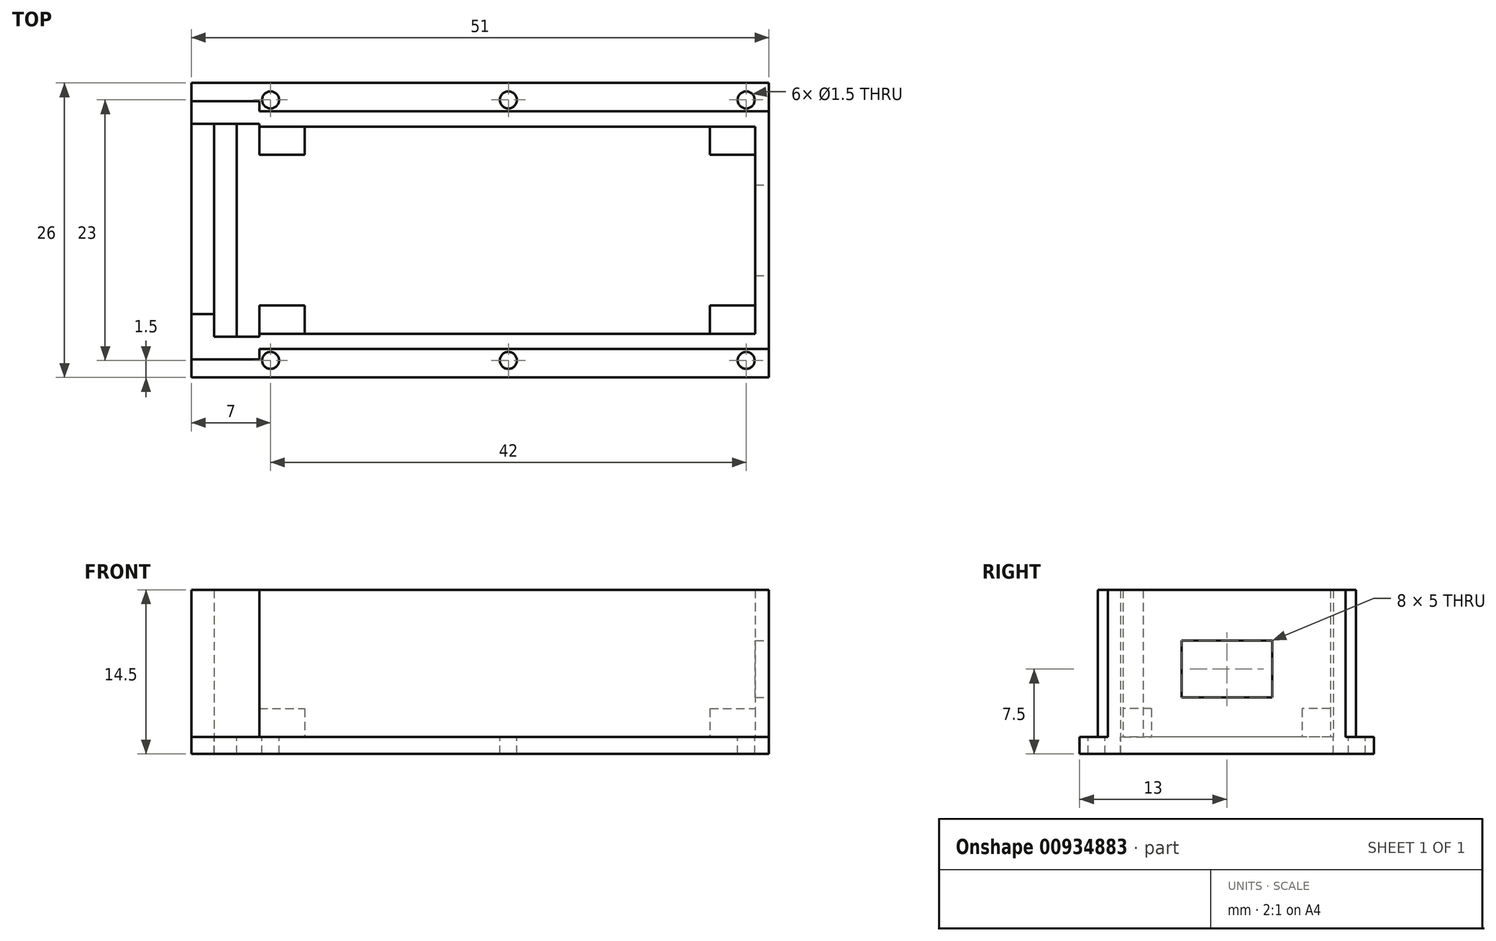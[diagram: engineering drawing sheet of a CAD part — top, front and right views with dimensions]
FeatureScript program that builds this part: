
annotation { "Feature Type Name" : "Feature", "Feature Type Description" : "" }
export const myFeature = defineFeature(function(context is Context, id is Id, definition is map)
    precondition{}
    {
        {
            var Q0;
            Q0=qCreatedBy(makeId("Top.planeOp"),FACE);
            var sketch = newSketch(context, id + "F0", { "sketchPlane" : qUnion([Q0])});
            skLineSegment(sketch, "E0.bottom", {"start": v(-25.5, 13) * mm, "end": v(25.5, 13) * mm});
            skLineSegment(sketch, "E0.top", {"start": v(-25.5, -13) * mm, "end": v(25.5, -13) * mm});
            skLineSegment(sketch, "E0.left", {"start": v(-25.5, 13) * mm, "end": v(-25.5, -13) * mm});
            skLineSegment(sketch, "E0.right", {"start": v(25.5, 13) * mm, "end": v(25.5, -13) * mm});
            skSolve(sketch);
        }
        {
            var Q0;
            Q0 = qSketchRegion(id + "F0", true);
            extrude(context, id + "F1", {"entities" : qUnion([Q0]), "depth" : 1.5 * mm, "offsetDistance" : 25 * mm});
        }
        {
            var Q0;
            Q0=makeQuery(id+"F1.opExtrude","CAP_FACE",FACE,{"disambiguationData":[OSD([sQuery(id+"F0.wireOp",EDGE,"E0.bottom"),sQuery(id+"F0.wireOp",EDGE,"E0.top"),sQuery(id+"F0.wireOp",EDGE,"E0.left"),sQuery(id+"F0.wireOp",EDGE,"E0.right")])],"isStart":false});
            var sketch = newSketch(context, id + "F2", { "sketchPlane" : qUnion([Q0])});
            skLineSegment(sketch, "E1.bottom", {"start": v(-25.5, 11.4) * mm, "end": v(-19.5, 11.4) * mm});
            skLineSegment(sketch, "E1.top", {"start": v(-25.5, 9.4) * mm, "end": v(-19.5, 9.4) * mm});
            skLineSegment(sketch, "E1.left", {"start": v(-25.5, 11.4) * mm, "end": v(-25.5, 9.4) * mm});
            skLineSegment(sketch, "E1.right", {"start": v(-19.5, 11.4) * mm, "end": v(-19.5, 9.4) * mm});
            skLineSegment(sketch, "E2.bottom", {"start": v(-25.5, 9.4) * mm, "end": v(-23.5, 9.4) * mm});
            skLineSegment(sketch, "E2.top", {"start": v(-25.5, 7.4) * mm, "end": v(-23.5, 7.4) * mm});
            skLineSegment(sketch, "E2.left", {"start": v(-25.5, 9.4) * mm, "end": v(-25.5, 7.4) * mm});
            skLineSegment(sketch, "E2.right", {"start": v(-23.5, 9.4) * mm, "end": v(-23.5, 7.4) * mm});
            skLineSegment(sketch, "E3.bottom", {"start": v(-21.5, 9.4) * mm, "end": v(-19.5, 9.4) * mm});
            skLineSegment(sketch, "E3.top", {"start": v(-21.5, 7.4) * mm, "end": v(-19.5, 7.4) * mm});
            skLineSegment(sketch, "E3.left", {"start": v(-21.5, 9.4) * mm, "end": v(-21.5, 7.4) * mm});
            skLineSegment(sketch, "E3.right", {"start": v(-19.5, 9.4) * mm, "end": v(-19.5, 7.4) * mm});
            skLineSegment(sketch, "E4.bottom", {"start": v(-25.5, -7.4) * mm, "end": v(-23.5, -7.4) * mm});
            skLineSegment(sketch, "E4.top", {"start": v(-25.5, -9.4) * mm, "end": v(-23.5, -9.4) * mm});
            skLineSegment(sketch, "E4.left", {"start": v(-25.5, -7.4) * mm, "end": v(-25.5, -9.4) * mm});
            skLineSegment(sketch, "E4.right", {"start": v(-23.5, -7.4) * mm, "end": v(-23.5, -9.4) * mm});
            skLineSegment(sketch, "E5.bottom", {"start": v(-25.5, -9.4) * mm, "end": v(-19.5, -9.4) * mm});
            skLineSegment(sketch, "E5.top", {"start": v(-25.5, -11.4) * mm, "end": v(-19.5, -11.4) * mm});
            skLineSegment(sketch, "E5.left", {"start": v(-25.5, -9.4) * mm, "end": v(-25.5, -11.4) * mm});
            skLineSegment(sketch, "E5.right", {"start": v(-19.5, -9.4) * mm, "end": v(-19.5, -11.4) * mm});
            skLineSegment(sketch, "E6.bottom", {"start": v(-21.5, -9.4) * mm, "end": v(-19.5, -9.4) * mm});
            skLineSegment(sketch, "E6.top", {"start": v(-21.5, -7.4) * mm, "end": v(-19.5, -7.4) * mm});
            skLineSegment(sketch, "E6.left", {"start": v(-21.5, -9.4) * mm, "end": v(-21.5, -7.4) * mm});
            skLineSegment(sketch, "E6.right", {"start": v(-19.5, -9.4) * mm, "end": v(-19.5, -7.4) * mm});
            skSolve(sketch);
        }
        {
            var Q0;
            Q0=makeQuery(id+"F2.imprint","IMPRINT",FACE,{"disambiguationData":[TD([[makeQuery(id+"F2.imprint","IMPRINT",EDGE,{"derivedFrom":sQuery(id+"F2.wireOp",EDGE,"E2.bottom")}),-1.0]])]});
            var Q1;
            Q1=makeQuery(id+"F2.imprint","IMPRINT",FACE,{"disambiguationData":[TD([[makeQuery(id+"F2.imprint","IMPRINT",EDGE,{"derivedFrom":sQuery(id+"F2.wireOp",EDGE,"E1.bottom")}),-1.0]])]});
            var Q2;
            Q2=makeQuery(id+"F2.imprint","IMPRINT",FACE,{"disambiguationData":[TD([[makeQuery(id+"F2.imprint","IMPRINT",EDGE,{"derivedFrom":sQuery(id+"F2.wireOp",EDGE,"E3.bottom")}),-1.0]])]});
            var Q3;
            Q3=makeQuery(id+"F2.imprint","IMPRINT",FACE,{"disambiguationData":[TD([[makeQuery(id+"F2.imprint","IMPRINT",EDGE,{"derivedFrom":sQuery(id+"F2.wireOp",EDGE,"E4.bottom")}),-1.0]])]});
            var Q4;
            Q4=makeQuery(id+"F2.imprint","IMPRINT",FACE,{"disambiguationData":[TD([[makeQuery(id+"F2.imprint","IMPRINT",EDGE,{"derivedFrom":sQuery(id+"F2.wireOp",EDGE,"E5.top")}),1.0]])]});
            var Q5;
            Q5=makeQuery(id+"F2.imprint","IMPRINT",FACE,{"disambiguationData":[TD([[makeQuery(id+"F2.imprint","IMPRINT",EDGE,{"derivedFrom":sQuery(id+"F2.wireOp",EDGE,"E6.bottom")}),1.0]])]});
            extrude(context, id + "F3", {"entities" : qUnion([Q0, Q1, Q2, Q3, Q4, Q5]), "operationType" : NewBodyOperationType.ADD, "depth" : 13 * mm, "offsetDistance" : 25 * mm});
        }
        {
            var Q0;
            Q0=makeQuery(id+"F1.opExtrude","CAP_FACE",FACE,{"disambiguationData":[OSD([sQuery(id+"F0.wireOp",EDGE,"E0.bottom"),sQuery(id+"F0.wireOp",EDGE,"E0.top"),sQuery(id+"F0.wireOp",EDGE,"E0.left"),sQuery(id+"F0.wireOp",EDGE,"E0.right")])],"isStart":false});
            var sketch = newSketch(context, id + "F4", { "sketchPlane" : qUnion([Q0])});
            skLineSegment(sketch, "E7.bottom", {"start": v(-19.5, 9.15) * mm, "end": v(24.3, 9.15) * mm});
            skLineSegment(sketch, "E7.top", {"start": v(-19.5, -9.15) * mm, "end": v(24.3, -9.15) * mm});
            skLineSegment(sketch, "E7.left", {"start": v(-19.5, 9.15) * mm, "end": v(-19.5, -9.15) * mm});
            skLineSegment(sketch, "E7.right", {"start": v(24.3, 9.15) * mm, "end": v(24.3, -9.15) * mm});
            skLineSegment(sketch, "E8.bottom", {"start": v(-19.5, 10.5) * mm, "end": v(25.5, 10.5) * mm});
            skLineSegment(sketch, "E8.top", {"start": v(-19.5, -10.5) * mm, "end": v(25.5, -10.5) * mm});
            skLineSegment(sketch, "E8.left", {"start": v(-19.5, 10.5) * mm, "end": v(-19.5, -10.5) * mm});
            skLineSegment(sketch, "E8.right", {"start": v(25.5, 10.5) * mm, "end": v(25.5, -10.5) * mm});
            skSolve(sketch);
        }
        {
            var Q0;
            {var subQ2=sQuery(id+"F4.wireOp",EDGE,"E7.bottom");Q0=makeQuery(id+"F4.imprint","IMPRINT",FACE,{"disambiguationData":[TD([[makeQuery(id+"F4.imprint","IMPRINT",EDGE,{"derivedFrom":subQ2}),1.0]])]});}
            extrude(context, id + "F5", {"entities" : qUnion([Q0]), "operationType" : NewBodyOperationType.ADD, "depth" : 13 * mm, "offsetDistance" : 25 * mm});
        }
        {
            var Q0;
            {var subQ0=sQuery(id+"F0.wireOp",EDGE,"E0.left");Q0=makeQuery(id+"F5.boolean.opBoolean","SPLIT",FACE,{"disambiguationData":[TD([makeQuery(id+"F3.opExtrude","SWEPT_FACE",FACE,{"disambiguationData":[OSD([sQuery(id+"F2.wireOp",EDGE,"E1.top")])]})])],"derivedFrom":makeQuery(id+"F1.opExtrude","CAP_FACE",FACE,{"disambiguationData":[OSD([sQuery(id+"F0.wireOp",EDGE,"E0.bottom"),sQuery(id+"F0.wireOp",EDGE,"E0.top"),subQ0,sQuery(id+"F0.wireOp",EDGE,"E0.right")])],"isStart":false})});}
            var sketch = newSketch(context, id + "F6", { "sketchPlane" : qUnion([Q0])});
            skLineSegment(sketch, "E9.bottom", {"start": v(-19.5, 9.15) * mm, "end": v(-15.5, 9.15) * mm});
            skLineSegment(sketch, "E9.top", {"start": v(-19.5, 6.65) * mm, "end": v(-15.5, 6.65) * mm});
            skLineSegment(sketch, "E9.left", {"start": v(-19.5, 9.15) * mm, "end": v(-19.5, 6.65) * mm});
            skLineSegment(sketch, "E9.right", {"start": v(-15.5, 9.15) * mm, "end": v(-15.5, 6.65) * mm});
            skLineSegment(sketch, "E10.bottom", {"start": v(24.3, 9.15) * mm, "end": v(20.3, 9.15) * mm});
            skLineSegment(sketch, "E10.top", {"start": v(24.3, 6.65) * mm, "end": v(20.3, 6.65) * mm});
            skLineSegment(sketch, "E10.left", {"start": v(24.3, 9.15) * mm, "end": v(24.3, 6.65) * mm});
            skLineSegment(sketch, "E10.right", {"start": v(20.3, 9.15) * mm, "end": v(20.3, 6.65) * mm});
            skLineSegment(sketch, "E11.bottom", {"start": v(24.3, -9.15) * mm, "end": v(20.3, -9.15) * mm});
            skLineSegment(sketch, "E11.top", {"start": v(24.3, -6.65) * mm, "end": v(20.3, -6.65) * mm});
            skLineSegment(sketch, "E11.left", {"start": v(24.3, -9.15) * mm, "end": v(24.3, -6.65) * mm});
            skLineSegment(sketch, "E11.right", {"start": v(20.3, -9.15) * mm, "end": v(20.3, -6.65) * mm});
            skLineSegment(sketch, "E12.bottom", {"start": v(-19.5, -9.15) * mm, "end": v(-15.5, -9.15) * mm});
            skLineSegment(sketch, "E12.top", {"start": v(-19.5, -6.65) * mm, "end": v(-15.5, -6.65) * mm});
            skLineSegment(sketch, "E12.left", {"start": v(-19.5, -9.15) * mm, "end": v(-19.5, -6.65) * mm});
            skLineSegment(sketch, "E12.right", {"start": v(-15.5, -9.15) * mm, "end": v(-15.5, -6.65) * mm});
            skSolve(sketch);
        }
        {
            var Q0;
            {var subQ2=sQuery(id+"F6.wireOp",EDGE,"E9.bottom");Q0=makeQuery(id+"F6.imprint","IMPRINT",FACE,{"disambiguationData":[TD([[makeQuery(id+"F6.imprint","IMPRINT",EDGE,{"derivedFrom":subQ2}),-1.0]])]});}
            var Q1;
            Q1=makeQuery(id+"F6.imprint","IMPRINT",FACE,{"disambiguationData":[TD([[makeQuery(id+"F6.imprint","IMPRINT",EDGE,{"derivedFrom":sQuery(id+"F6.wireOp",EDGE,"E10.bottom")}),-1.0]])]});
            var Q2;
            Q2=makeQuery(id+"F6.imprint","IMPRINT",FACE,{"disambiguationData":[TD([[makeQuery(id+"F6.imprint","IMPRINT",EDGE,{"derivedFrom":sQuery(id+"F6.wireOp",EDGE,"E11.bottom")}),1.0]])]});
            var Q3;
            {var subQ3=sQuery(id+"F6.wireOp",EDGE,"E12.bottom");Q3=makeQuery(id+"F6.imprint","IMPRINT",FACE,{"disambiguationData":[TD([[makeQuery(id+"F6.imprint","IMPRINT",EDGE,{"derivedFrom":subQ3}),1.0]])]});}
            extrude(context, id + "F7", {"entities" : qUnion([Q0, Q1, Q2, Q3]), "operationType" : NewBodyOperationType.ADD, "depth" : 2.5 * mm, "offsetDistance" : 25 * mm});
        }
        {
            var Q0;
            {var subQ0=sQuery(id+"F0.wireOp",EDGE,"E0.left");var subQ1=sQuery(id+"F0.wireOp",EDGE,"E0.bottom");var subQ2=sQuery(id+"F0.wireOp",EDGE,"E0.right");var subQ3=sQuery(id+"F0.wireOp",EDGE,"E0.top");Q0=makeQuery(id+"F5.boolean.opBoolean","SPLIT",FACE,{"disambiguationData":[TD([makeQuery(id+"F1.opExtrude","SWEPT_FACE",FACE,{"disambiguationData":[OSD([subQ1])]})])],"derivedFrom":makeQuery(id+"F1.opExtrude","CAP_FACE",FACE,{"disambiguationData":[OSD([subQ1,subQ3,subQ0,subQ2])],"isStart":false})});}
            var sketch = newSketch(context, id + "F8", { "sketchPlane" : qUnion([Q0])});
            skCircle(sketch, "E13", {"center": v(-18.5, 11.5) * mm, "radius": 0.75 * mm});
            skCircle(sketch, "E14", {"center": v(-18.5, -11.5) * mm, "radius": 0.75 * mm});
            skCircle(sketch, "E15.1.0.0", {"center": v(2.5, 11.5) * mm, "radius": 0.75 * mm});
            skCircle(sketch, "E15.2.0.0", {"center": v(23.5, 11.5) * mm, "radius": 0.75 * mm});
            skLineSegment(sketch, "E15.direction1", {"start": v(-18.5, 11.5) * mm, "end": v(2.5, 11.5) * mm, "construction": true});
            skCircle(sketch, "E16.1.0.0", {"center": v(2.5, -11.5) * mm, "radius": 0.75 * mm});
            skCircle(sketch, "E16.2.0.0", {"center": v(23.5, -11.5) * mm, "radius": 0.75 * mm});
            skLineSegment(sketch, "E16.direction1", {"start": v(-18.5, -11.5) * mm, "end": v(2.5, -11.5) * mm, "construction": true});
            skSolve(sketch);
        }
        {
            var Q0;
            Q0=makeQuery(id+"F8.imprint","IMPRINT",FACE,{"disambiguationData":[TD([[makeQuery(id+"F8.imprint","IMPRINT",EDGE,{"derivedFrom":sQuery(id+"F8.wireOp",EDGE,"E13")}),1.0]])]});
            var Q1;
            Q1=makeQuery(id+"F8.imprint","IMPRINT",FACE,{"disambiguationData":[TD([[makeQuery(id+"F8.imprint","IMPRINT",EDGE,{"derivedFrom":sQuery(id+"F8.wireOp",EDGE,"E15.1.0.0")}),1.0]])]});
            var Q2;
            Q2=makeQuery(id+"F8.imprint","IMPRINT",FACE,{"disambiguationData":[TD([[makeQuery(id+"F8.imprint","IMPRINT",EDGE,{"derivedFrom":sQuery(id+"F8.wireOp",EDGE,"E15.2.0.0")}),1.0]])]});
            var Q3;
            Q3=makeQuery(id+"F8.imprint","IMPRINT",FACE,{"disambiguationData":[TD([[makeQuery(id+"F8.imprint","IMPRINT",EDGE,{"derivedFrom":sQuery(id+"F8.wireOp",EDGE,"E14")}),1.0]])]});
            var Q4;
            Q4=makeQuery(id+"F8.imprint","IMPRINT",FACE,{"disambiguationData":[TD([[makeQuery(id+"F8.imprint","IMPRINT",EDGE,{"derivedFrom":sQuery(id+"F8.wireOp",EDGE,"E16.1.0.0")}),1.0]])]});
            var Q5;
            Q5=makeQuery(id+"F8.imprint","IMPRINT",FACE,{"disambiguationData":[TD([[makeQuery(id+"F8.imprint","IMPRINT",EDGE,{"derivedFrom":sQuery(id+"F8.wireOp",EDGE,"E16.2.0.0")}),1.0]])]});
            extrude(context, id + "F9", {"entities" : qUnion([Q0, Q1, Q2, Q3, Q4, Q5]), "operationType" : NewBodyOperationType.REMOVE, "endBound" : BoundingType.THROUGH_ALL, "oppositeDirection" : true, "depth" : 25 * mm, "offsetDistance" : 25 * mm});
        }
        {
            var Q0;
            {var subQ0=sQuery(id+"F0.wireOp",EDGE,"E0.left");Q0=makeQuery(id+"F5.boolean.opBoolean","SPLIT",FACE,{"disambiguationData":[TD([makeQuery(id+"F3.opExtrude","SWEPT_FACE",FACE,{"disambiguationData":[OSD([sQuery(id+"F2.wireOp",EDGE,"E1.top")])]})])],"derivedFrom":makeQuery(id+"F1.opExtrude","CAP_FACE",FACE,{"disambiguationData":[OSD([sQuery(id+"F0.wireOp",EDGE,"E0.bottom"),sQuery(id+"F0.wireOp",EDGE,"E0.top"),subQ0,sQuery(id+"F0.wireOp",EDGE,"E0.right")])],"isStart":false})});}
            var sketch = newSketch(context, id + "F10", { "sketchPlane" : qUnion([Q0])});
            skLineSegment(sketch, "E17.bottom", {"start": v(-23.5, 9.4) * mm, "end": v(-21.5, 9.4) * mm});
            skLineSegment(sketch, "E17.top", {"start": v(-23.5, -9.4) * mm, "end": v(-21.5, -9.4) * mm});
            skLineSegment(sketch, "E17.left", {"start": v(-23.5, 9.4) * mm, "end": v(-23.5, -9.4) * mm});
            skLineSegment(sketch, "E17.right", {"start": v(-21.5, 9.4) * mm, "end": v(-21.5, -9.4) * mm});
            skSolve(sketch);
        }
        {
            var Q0;
            {var subQ1=sQuery(id+"F10.wireOp",EDGE,"E17.bottom");Q0=makeQuery(id+"F10.imprint","IMPRINT",FACE,{"disambiguationData":[TD([[makeQuery(id+"F10.imprint","IMPRINT",EDGE,{"derivedFrom":subQ1}),-1.0]])]});}
            extrude(context, id + "F11", {"entities" : qUnion([Q0]), "operationType" : NewBodyOperationType.REMOVE, "oppositeDirection" : true, "depth" : 2 * mm, "offsetDistance" : 25 * mm});
        }
        {
            var Q0;
            Q0=makeQuery(id+"F5.opExtrude","SWEPT_FACE",FACE,{"disambiguationData":[OSD([sQuery(id+"F4.wireOp",EDGE,"E8.right")])]});
            var sketch = newSketch(context, id + "F12", { "sketchPlane" : qUnion([Q0])});
            skLineSegment(sketch, "E18.bottom", {"start": v(-4, 10) * mm, "end": v(4, 10) * mm});
            skLineSegment(sketch, "E18.top", {"start": v(-4, 5) * mm, "end": v(4, 5) * mm});
            skLineSegment(sketch, "E18.left", {"start": v(-4, 10) * mm, "end": v(-4, 5) * mm});
            skLineSegment(sketch, "E18.right", {"start": v(4, 10) * mm, "end": v(4, 5) * mm});
            skSolve(sketch);
        }
        {
            var Q0;
            Q0=makeQuery(id+"F12.imprint","IMPRINT",FACE,{"disambiguationData":[TD([[makeQuery(id+"F12.imprint","IMPRINT",EDGE,{"derivedFrom":sQuery(id+"F12.wireOp",EDGE,"E18.bottom")}),-1.0]])]});
            extrude(context, id + "F13", {"entities" : qUnion([Q0]), "operationType" : NewBodyOperationType.REMOVE, "endBound" : BoundingType.UP_TO_NEXT, "oppositeDirection" : true, "depth" : 25 * mm, "offsetDistance" : 25 * mm});
        }
    });
